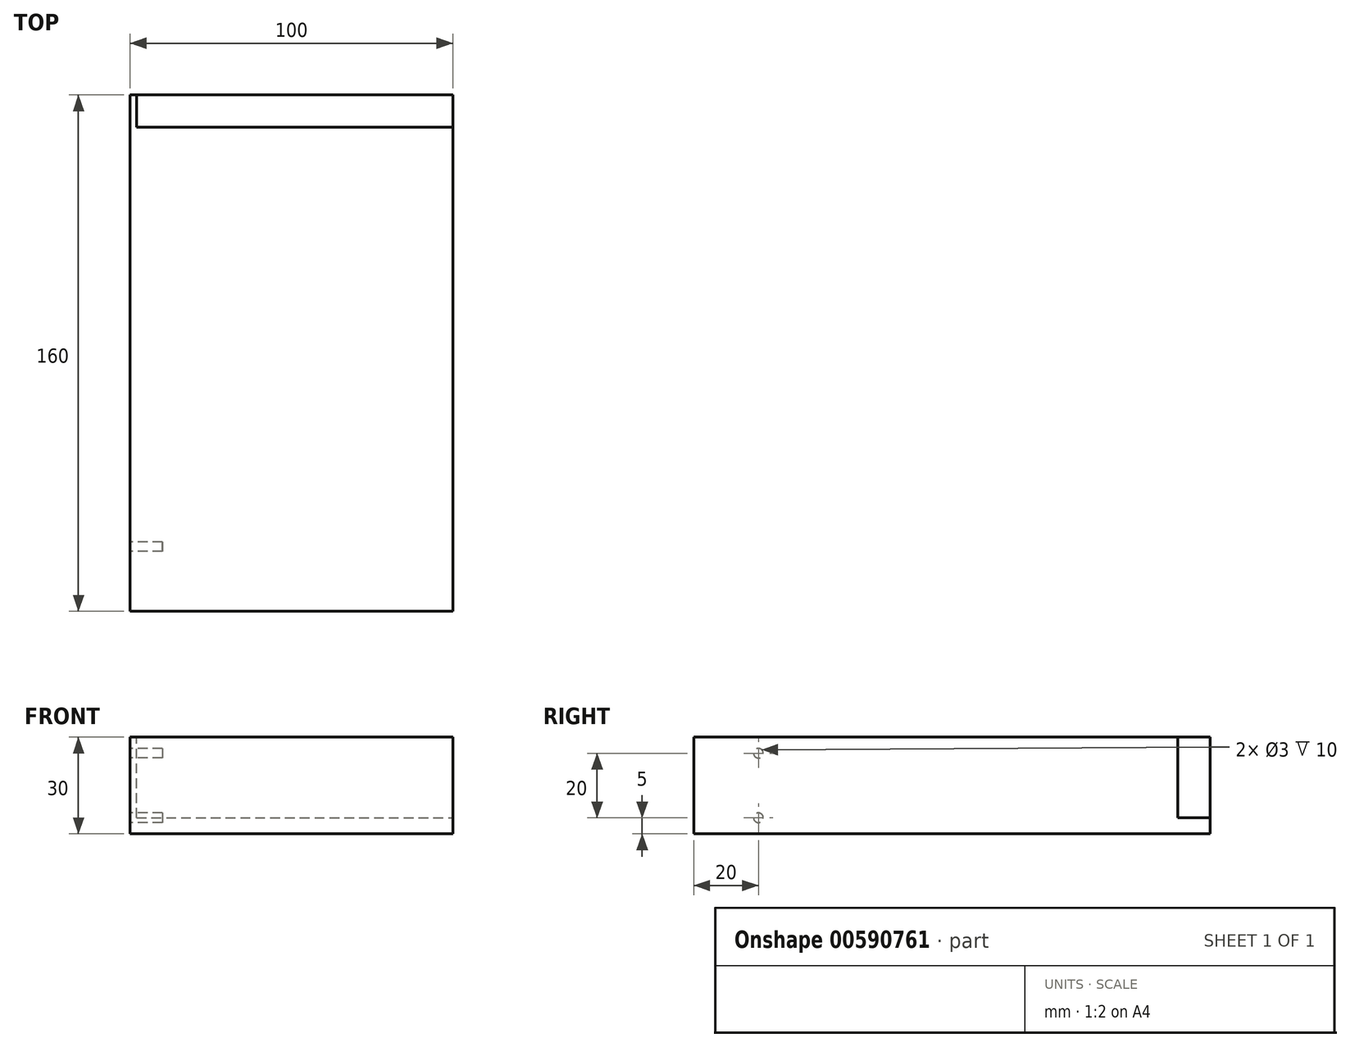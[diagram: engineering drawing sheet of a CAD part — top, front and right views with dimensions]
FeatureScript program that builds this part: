
annotation { "Feature Type Name" : "Feature", "Feature Type Description" : "" }
export const myFeature = defineFeature(function(context is Context, id is Id, definition is map)
    precondition{}
    {
        {
            var Q0;
            Q0=qCreatedBy(makeId("Top.planeOp"),FACE);
            var sketch = newSketch(context, id + "F0", { "sketchPlane" : qUnion([Q0])});
            skLineSegment(sketch, "E0.bottom", {"start": v(0, 0) * mm, "end": v(100, 0) * mm});
            skLineSegment(sketch, "E0.top", {"start": v(0, -160) * mm, "end": v(100, -160) * mm});
            skLineSegment(sketch, "E0.left", {"start": v(0, 0) * mm, "end": v(0, -160) * mm});
            skLineSegment(sketch, "E0.right", {"start": v(100, 0) * mm, "end": v(100, -160) * mm});
            skSolve(sketch);
        }
        {
            var Q0;
            Q0 = qSketchRegion(id + "F0", true);
            extrude(context, id + "F1", {"entities" : qUnion([Q0]), "depth" : 30 * mm, "offsetDistance" : 25.4 * mm});
        }
        {
            var Q0;
            Q0=makeQuery(id+"F1.opExtrude","SWEPT_FACE",FACE,{"disambiguationData":[OSD([sQuery(id+"F0.wireOp",EDGE,"E0.left")])]});
            var sketch = newSketch(context, id + "F2", { "sketchPlane" : qUnion([Q0])});
            skCircle(sketch, "E1", {"center": v(140, 25) * mm, "radius": 1.5 * mm});
            skCircle(sketch, "E2", {"center": v(140, 5) * mm, "radius": 1.5 * mm});
            skSolve(sketch);
        }
        {
            var Q0;
            Q0=makeQuery(id+"F2.imprint","IMPRINT",FACE,{"disambiguationData":[TD([[makeQuery(id+"F2.imprint","IMPRINT",EDGE,{"derivedFrom":sQuery(id+"F2.wireOp",EDGE,"E1")}),1.0]])]});
            var Q1;
            Q1=makeQuery(id+"F2.imprint","IMPRINT",FACE,{"disambiguationData":[TD([[makeQuery(id+"F2.imprint","IMPRINT",EDGE,{"derivedFrom":sQuery(id+"F2.wireOp",EDGE,"E2")}),1.0]])]});
            extrude(context, id + "F3", {"entities" : qUnion([Q0, Q1]), "operationType" : NewBodyOperationType.REMOVE, "oppositeDirection" : true, "depth" : 10 * mm, "offsetDistance" : 25 * mm});
        }
        {
            var Q0;
            Q0=makeQuery(id+"F1.opExtrude","CAP_FACE",FACE,{"disambiguationData":[OSD([sQuery(id+"F0.wireOp",EDGE,"E0.bottom"),sQuery(id+"F0.wireOp",EDGE,"E0.top"),sQuery(id+"F0.wireOp",EDGE,"E0.left"),sQuery(id+"F0.wireOp",EDGE,"E0.right")])],"isStart":false});
            var sketch = newSketch(context, id + "F4", { "sketchPlane" : qUnion([Q0])});
            skLineSegment(sketch, "E3.bottom", {"start": v(100, 0) * mm, "end": v(2, 0) * mm});
            skLineSegment(sketch, "E3.top", {"start": v(100, -10) * mm, "end": v(2, -10) * mm});
            skLineSegment(sketch, "E3.left", {"start": v(100, 0) * mm, "end": v(100, -10) * mm});
            skLineSegment(sketch, "E3.right", {"start": v(2, 0) * mm, "end": v(2, -10) * mm});
            skSolve(sketch);
        }
        {
            var Q0;
            Q0=makeQuery(id+"F4.imprint","IMPRINT",FACE,{"disambiguationData":[TD([[makeQuery(id+"F4.imprint","IMPRINT",EDGE,{"derivedFrom":sQuery(id+"F4.wireOp",EDGE,"E3.bottom")}),-1.0]])]});
            extrude(context, id + "F5", {"entities" : qUnion([Q0]), "operationType" : NewBodyOperationType.REMOVE, "oppositeDirection" : true, "depth" : 25 * mm, "offsetDistance" : 25 * mm});
        }
    });
